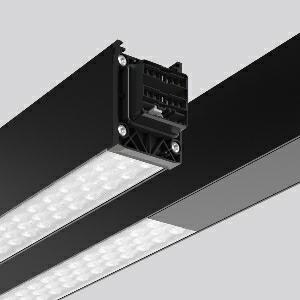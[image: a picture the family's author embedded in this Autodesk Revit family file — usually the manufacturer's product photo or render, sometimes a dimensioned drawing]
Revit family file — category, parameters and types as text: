
# Revit family: linedo_2_3m_30_1100_952330_853_400_503_b701
name_source: partatom
category: Lighting Fixtures
units: mm (PartAtom-declared; Revit-internal decimal feet)

## family parameters
Cut with Voids When Loaded = No
Host = Face
Light Source = No
Part Type = Normal
Room Calculation Point = No
Round Connector Dimension = Use Diameter
Shared = No

## types (1)
- LINEDO_2,3m_30_1100 (1 x LED Modul 850, 4100 lm, 5000)
    Apparent Load = 55 VA
    CIE Flux Codes = 89 97 99 100 100
    Color Rendering = 80
    Color Temperature = 5000
    Default Elevation = 1800 mm
    Description = LINEDO, 55 W, 8200 lm, 850, black, on/off
Continuous line luminaire, L 2291 B 58 H 76
    Height = 76 mm
    Lamp = 1 x LED Modul 850
    Lamp Light Flux = 4100 lm
    Lamp count = 1
    Length = 2291 mm
    Lifetime = 50000 h
    Luminous efficacy = 149 lm/W
    Manufacturer = RZB
    ModVariant = No
    Model = 952330.853.400.503
    Mounting Place = Ceiling
    Mounting Type = Surface mounted, Pendant
    Number of Poles = 1
    OnlyDefault = Yes
    Power Factor = 1
    Product Name = LINEDO_2,3m_30_1100
    Product group = Continuous line luminaire system Linedo IP 54
    ProductGroupID = 314
    Protection Class = Protection class I
    Protection Degree = IP 54
    RLX_Detail_Level = 1
    RLX_Emergency_Light_Flux = 0 lm
    RLX_Emergency_Type = 0
    RLX_Emergency_Type_DB = No
    RlxData = <blob elided: 56589 chars, md5=ffbc3e5c>
    Socket = socket
    Standby Power = 0 W
    System Light Flux = 8200 lm
    System Power = 55 W
    Type Comments = Product without accessories
    Type Image = 954530.853.476.504.jpg
    URL = http://relux.com
    VarID = ---
    Voltage = 230 V
    Voltage Range = 220-240 V
    Weight = 0.00 kg
    Width = 58 mm

## geometry (parser evidence)
native form markers: Blend x4, Sweep x18
no freeform markers — native parametric forms only
